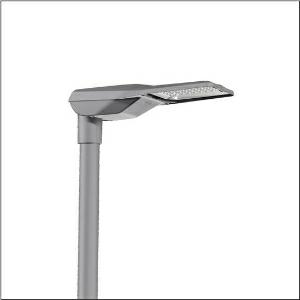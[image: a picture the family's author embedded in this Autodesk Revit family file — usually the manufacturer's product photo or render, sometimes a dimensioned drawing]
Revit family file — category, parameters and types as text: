
# Revit family: streetlight_sl_21_iq_mini___st1_5a_5xe2p41d08hb_72ee
name_source: partatom
category: Lighting Fixtures
units: mm (PartAtom-declared; Revit-internal decimal feet)

## family parameters
Cut with Voids When Loaded = No
Host = Face
Light Source = No
Part Type = Normal
Room Calculation Point = No
Round Connector Dimension = Use Diameter
Shared = No

## types (1)
- --- (1 x LED, 9690 lm, 70.9 W, 4000K)
    Apparent Load = 71 VA
    CIE Flux Codes = 22 53 95 100 100
    Color Rendering = 70
    Color Temperature = 4000K
    Default Elevation = 1800 mm
    Description = Streetlight SL 21 iQ mini, mast luminaire, primary light control with lens, of PMMA, primary optical cover: cover, of toughened safety glass, transparent, light distribution: ST1.5a, light emission: direct distribution, primary light characteristic: asymmetric, installation type: post-top, side-entry, LED, High Power LED, rated luminous flux: 9.690lm, luminous efficacy: 137lm/W, light colour: 740, colour temperature: 4000K, control gear: iQ-Comfort, control: Auto-Match, Temp-Guard, Lumen-Switch, Night-Set, Smart-Wire, Light-Fading, Desk-Remote (wireless, voltage-free reading and setting of iQ features in the workshop via application-optimized NFC function/RFID function), optimised constant luminous flux control (CLO 2.0), pre-setting: linear dimming characteristic, mains connection: 220..240V, AC, 50/60Hz, start of lifetime: 71W, end of service life: 75W, reduction: 31W, luminaire housing, of diecast aluminium, powder-coated, Siteco® metallic grey (DB 702S), corrosivity category C5 mid according to DIN EN ISO 12944, please order mast flange separately, inclination adjustable: 0°, 5°, 10°, 15°, sealing non-destructively replaceable, multi-level sealing system, length: 628mm, width: 235mm, height: 110mm, mast flange for spigot size: 42mm (side-entry): 5XC10008XM4, 60/48mm (side-entry/post-top): 5XC10108XM2, 76/60mm (side-entry/post-top): 5XC10108XM1, mounting height: 4..8m, protection rating (complete): IP66, insulation class (complete): insulation class II (safety insulation), certification: CE, ENEC, ENEC+, VDE, impact resistance: IK10, permissible operating ambient temperature for outdoor applications: -40..+50°C, standard-compliant lighting for roads and squares, packaging unit: 1 piece

Light Distribution: ST1.5a
    Height = 110 mm
    Lamp = 1 x LED
    Lamp Light Flux = 9690 lm
    Lamp Power = 70.9 W
    Lamp count = 1
    Length = 625 mm
    Luminous efficacy = 137 lm/W
    Manufacturer = Siteco
    ModVariant = No
    Model = 5XE2P41D08HB
    Number of Poles = 1
    OnlyDefault = Yes
    Power Factor = 1
    Product Name = Streetlight SL 21 iQ mini | ST1.5a
    Product group = mast luminaire | pylon top
    ProductGroupID = 6100
    Protection Class = Protection class II
    Protection Degree = IP 66
    RLX_Detail_Level = 1
    RLX_Emergency_Light_Flux = 0 lm
    RLX_Emergency_Type = 0
    RLX_Emergency_Type_DB = No
    RlxData = <blob elided: 29829 chars, md5=ae3849c3>
    Socket = socket
    Standby Power = 0 W
    System Light Flux = 9690 lm
    System Power = 71 W
    Type Comments = factory setting: luminous flux: 100 % | dim-lin: 254 | 711 mA
    Type Image = l_1003519.jpg
    URL = http://relux.com
    VarID = @adj_157048
    Voltage = 0 V
    Weight = 0.00 kg
    Width = 234 mm

## geometry (parser evidence)
native form markers: Blend x4, Sweep x9
no freeform markers — native parametric forms only
